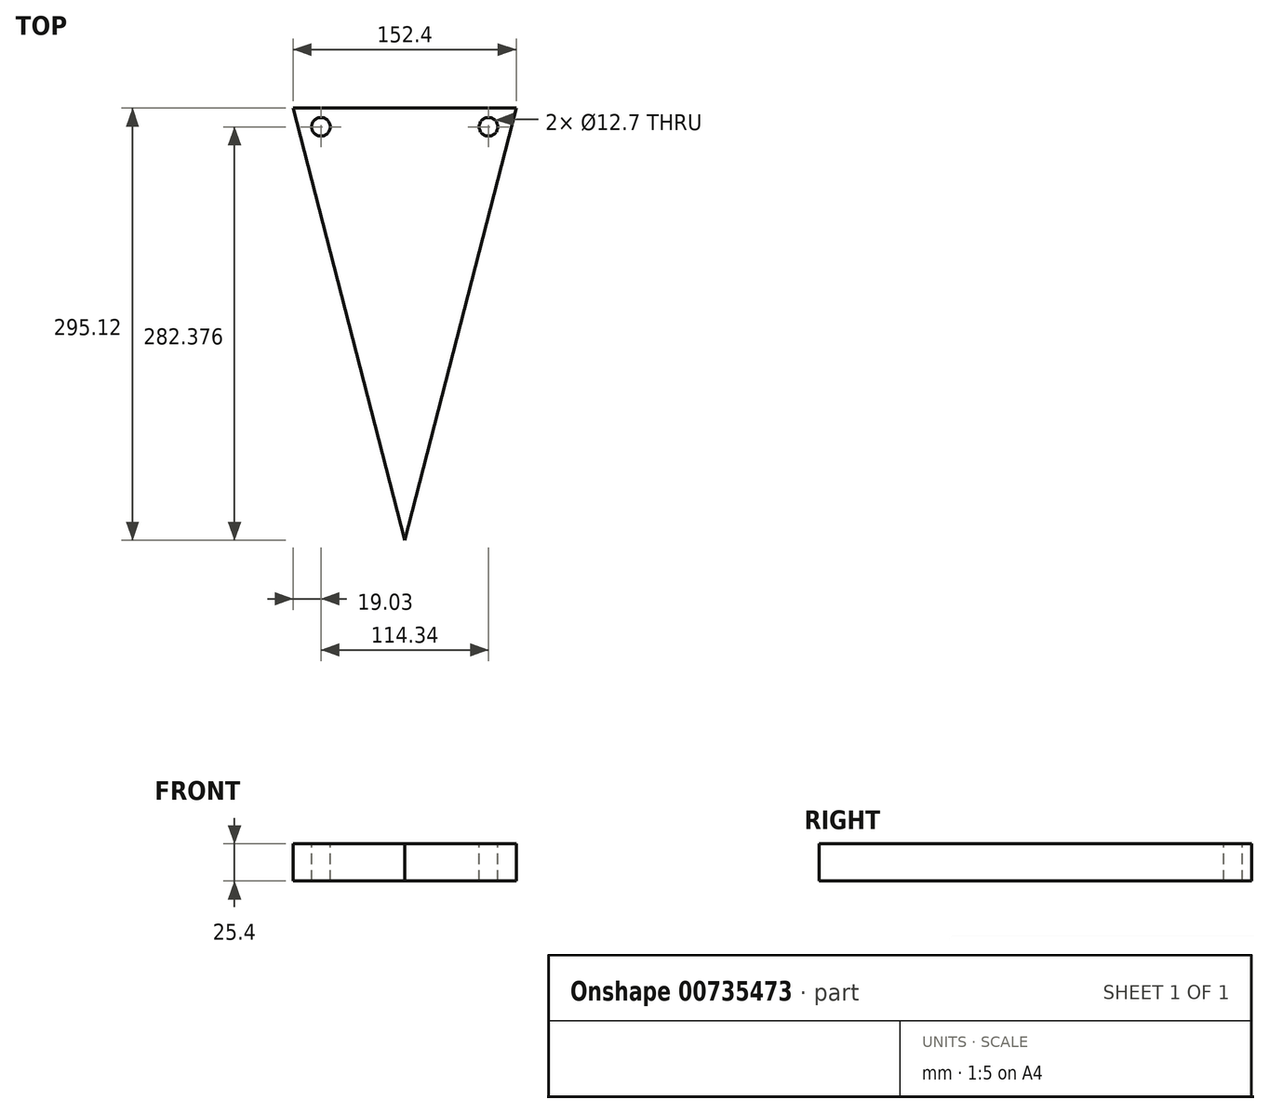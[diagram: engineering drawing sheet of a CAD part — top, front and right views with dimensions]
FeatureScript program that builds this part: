
annotation { "Feature Type Name" : "Feature", "Feature Type Description" : "" }
export const myFeature = defineFeature(function(context is Context, id is Id, definition is map)
    precondition{}
    {
        {
            var Q0;
            Q0=qCreatedBy(makeId("Top.planeOp"),FACE);
            var sketch = newSketch(context, id + "F0", { "sketchPlane" : qUnion([Q0])});
            skLineSegment(sketch, "E0", {"start": v(-76.2, 177.24) * mm, "end": v(76.2, 177.24) * mm});
            skLineSegment(sketch, "E1", {"start": v(-76.2, 177.24) * mm, "end": v(0, -117.88) * mm});
            skLineSegment(sketch, "E2", {"start": v(0, -117.88) * mm, "end": v(76.2, 177.24) * mm});
            skSolve(sketch);
        }
        {
            var Q0;
            Q0 = qSketchRegion(id + "F0", true);
            extrude(context, id + "F1", {"entities" : qUnion([Q0]), "depth" : 25.4 * mm, "offsetDistance" : 25.4 * mm});
        }
        {
            var Q0;
            Q0=makeQuery(id+"F1.opExtrude","CAP_FACE",FACE,{"disambiguationData":[OSD([sQuery(id+"F0.wireOp",EDGE,"E0"),sQuery(id+"F0.wireOp",EDGE,"E1"),sQuery(id+"F0.wireOp",EDGE,"E2")])],"isStart":false});
            var sketch = newSketch(context, id + "F2", { "sketchPlane" : qUnion([Q0])});
            skCircle(sketch, "E3", {"center": v(-57.17, 164.5) * mm, "radius": 6.35 * mm});
            skCircle(sketch, "E4", {"center": v(57.17, 164.5) * mm, "radius": 6.35 * mm});
            skSolve(sketch);
        }
        {
            var Q0;
            Q0=makeQuery(id+"F2.imprint","IMPRINT",FACE,{"disambiguationData":[TD([[makeQuery(id+"F2.imprint","IMPRINT",EDGE,{"derivedFrom":sQuery(id+"F2.wireOp",EDGE,"E3")}),1.0]])]});
            var Q1;
            Q1=makeQuery(id+"F2.imprint","IMPRINT",FACE,{"disambiguationData":[TD([[makeQuery(id+"F2.imprint","IMPRINT",EDGE,{"derivedFrom":sQuery(id+"F2.wireOp",EDGE,"E4")}),1.0]])]});
            extrude(context, id + "F3", {"entities" : qUnion([Q0, Q1]), "operationType" : NewBodyOperationType.REMOVE, "oppositeDirection" : true, "depth" : 25.4 * mm, "offsetDistance" : 25.4 * mm});
        }
    });
